# Revit family: Accessory-Shower_Rod-KOHLER-Expanse-K-9350_1
name_source: partatom
category: Specialty Equipment
revit_build: Autodesk Revit 2017 (Build: 20160225_1515(x64)
units: mm (PartAtom-declared; Revit-internal decimal feet)

## family parameters
Cut with Voids When Loaded = No
Host = Face
OmniClass Number = 23.31.25.00
OmniClass Title = Toilet and Bath Specialties
Part Type = Normal
Room Calculation Point = No
Round Connector Dimension = Use Diameter
Shared = No

## types (3) — shared parameters
ADA Compliant = No
Assembly Code = C1030200
Date Modified = 03/25/2020
Default Elevation = 42"
Description = Curved shower rod - transitional design
Height = 6"
Length = 76"
Manufacturer = KOHLER Co.
Master Format 2014 = 10 28 00
Master Format 2014 Name = Toilet, Bath, and Laundry Accessories
Material = Stainless Steel Construction
Product Documentation Link = https://www.us.kohler.com
Product Name = Expanse
Product Page URL = http://www.us.kohler.com
URL = https://www.us.kohler.com
WaterSense Certified = No
Width = 2 13/16"

## per-type parameters (varying)
| type | Finish | Model | Type |
| S-Polished Stainless | Kohler-Metal-S-Polished_Stainless | K-9350-S | 1 |
| BS-Brushed Stainless | Kohler-Metal-BS-Brushed_Stainless | K-9350-BS | 2 |
| 2BZ-Oil-Rubbed Bronze | Kohler-Metal-2BZ-Oil_Rubbed_Bronze | K-9350-2BZ | 3 |

## geometry (parser evidence)
native form markers: Sweep x6
no freeform markers — native parametric forms only
